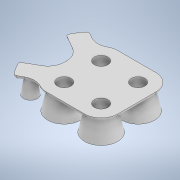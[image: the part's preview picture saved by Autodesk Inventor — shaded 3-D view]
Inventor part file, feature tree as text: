
AUTODESK INVENTOR PART (.ipt)
format: ipt  version: 2021 (Build 250183000, 183)  size: 701,440 bytes
history: native  units: mm
features: other x3, extrude x2, sketch x2, fillet x1
ambient origin geometry x8: Origin, YZ Plane, XZ Plane, XY Plane, X Axis, Y Axis, Z Axis, Center Point
bodies: Solid1 (feature_tree)
feature tree (8):
  other  "Soyuz Core Stage Part 1.ipt"
  extrude  "Extrusion1"  Depth=4.2mm
  fillet  "Fillet1"  Radius=4.2mm
  extrude  "Extrusion2"  Depth=4.2mm
  other  "Soyuz Booster::Soyuz Core Stage Part 1.ipt"
  other  "TaggingFeature1"
  sketch  "Sketch1"  dims[d0=10.0mm d5=4.2mm d6=4.2mm]
  sketch  "Sketch2"  dims[d7=4.2mm d8=4.2mm d9=4.0mm d11=120.0deg d12=120.0deg d13=120.0deg d14=120.0deg d15=1.0mm d16=1.0mm d17=0.0mm d18=0.0mm d19=1.0mm d20=1.0mm d22=0.0mm d23=0.0mm d25=1.0mm d26=120.0deg d27=0.0mm d29=0.0mm d30=0.0mm d32=1.0mm d33=4.0mm d34=0.5mm d39=0.0mm d40=0.0mm d41=0.0mm d42=0.0mm d43=0.0mm d44=0.0mm d45=0.0mm d46=0.0mm d48=0.0mm d49=0.0mm d50=0.0mm d51=0.0mm d52=1.0mm d53=0.0mm d54=1.0mm d55=0.0mm d56=0.0mm d57=7.0mm d58=0.0mm d59=0.0mm d4=0.5mm]
